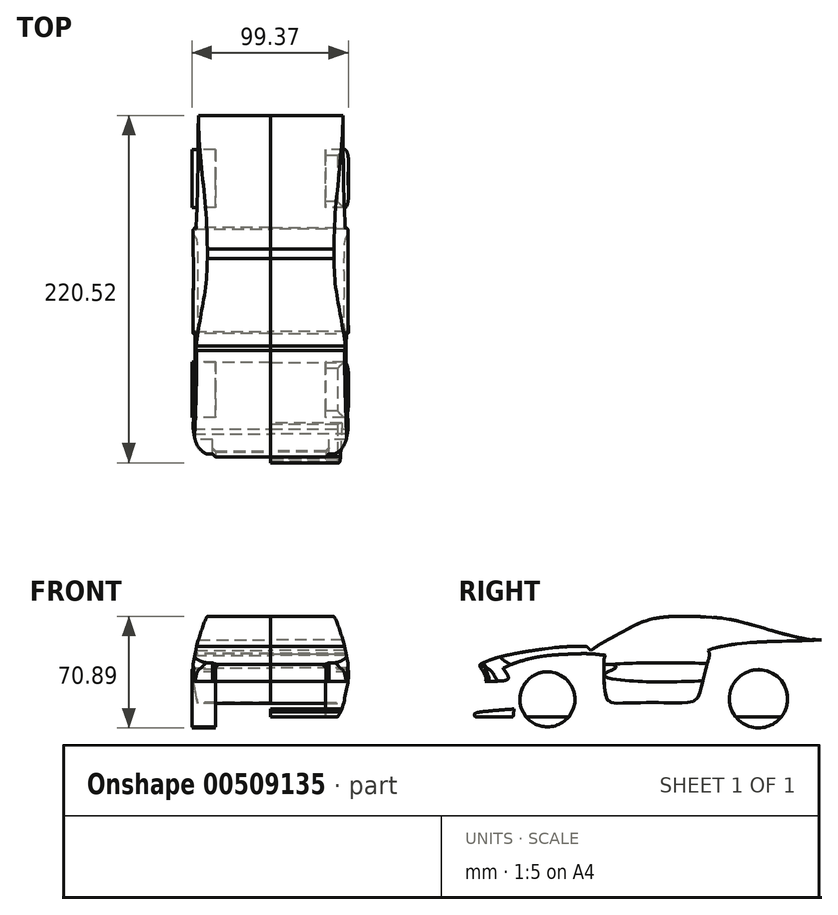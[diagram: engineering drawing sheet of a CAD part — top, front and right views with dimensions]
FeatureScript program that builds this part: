
annotation { "Feature Type Name" : "Feature", "Feature Type Description" : "" }
export const myFeature = defineFeature(function(context is Context, id is Id, definition is map)
    precondition{}
    {
        {
            var Q0;
            Q0=qCreatedBy(makeId("Right.planeOp"),FACE);
            var sketch = newSketch(context, id + "F0", { "sketchPlane" : qUnion([Q0])});
            skFitSpline(sketch, "E0", {"points": [v(-115.12, 3.89) * mm, v(-110.53, 5.87) * mm, v(-104.21, 8.1) * mm, v(-95.3, 10.2) * mm, v(-89.47, 11.32) * mm, v(-81.92, 12.56) * mm, v(-71.02, 14.05) * mm, v(-60.11, 15.04) * mm, v(-47.6, 15.16) * mm], "startDerivative": vector(46.35, 20.6) * mm, "endDerivative": vector(83.86, -0.63) * mm});
            skFitSpline(sketch, "E1", {"points": [v(-115.12, 3.89) * mm, v(-115.12, 2.28) * mm, v(-113.63, 0) * mm, v(-112.27, -2.68) * mm, v(-111.4, -5.03) * mm, v(-112.02, -6.89) * mm, v(-115.12, -7.26) * mm, v(-117.1, -8) * mm, v(-117.6, -10.98) * mm, v(-116.85, -14.07) * mm, v(-115.12, -17.91) * mm, v(-113.63, -22.75) * mm, v(-113.63, -25.84) * mm, v(-118.46, -27.45) * mm, v(-118.46, -29.19) * mm, v(-116.23, -29.44) * mm], "startDerivative": vector(-5.56, -32) * mm, "endDerivative": vector(44.62, 5.26) * mm});
            skFitSpline(sketch, "E2", {"points": [v(-116.23, -29.44) * mm, v(-112.64, -29.44) * mm, v(-107.06, -29.44) * mm, v(-97.77, -29.44) * mm, v(-94.18, -29.44) * mm], "startDerivative": vector(16.96, 0) * mm, "endDerivative": vector(14.87, 0) * mm});
            skLineSegment(sketch, "E3", {"start": v(-94.18, -29.44) * mm, "end": v(-92.7, -17.17) * mm});
            skArc(sketch, "E4", {"start": v(-92.7, -17.17) * mm, "mid": v(-71.99, 0.79) * mm, "end": v(-52.06, -18.04) * mm});
            skLineSegment(sketch, "E5", {"start": v(-52.06, -18.04) * mm, "end": v(-51.2, -29.07) * mm});
            skLineSegment(sketch, "E6", {"start": v(-51.2, -29.07) * mm, "end": v(-6.1, -29.07) * mm});
            skLineSegment(sketch, "E7", {"start": v(-6.1, -29.07) * mm, "end": v(31.32, -29.07) * mm});
            skLineSegment(sketch, "E8", {"start": v(31.32, -29.07) * mm, "end": v(40.99, -28.04) * mm});
            skLineSegment(sketch, "E9", {"start": v(40.99, -28.04) * mm, "end": v(40.99, -17.13) * mm});
            skArc(sketch, "E10", {"start": v(40.99, -17.13) * mm, "mid": v(61.47, 3.54) * mm, "end": v(82.33, -16.75) * mm});
            skLineSegment(sketch, "E11", {"start": v(82.33, -16.75) * mm, "end": v(83.68, -23.62) * mm});
            skLineSegment(sketch, "E12", {"start": v(83.68, -23.62) * mm, "end": v(106.37, -19.15) * mm});
            skLineSegment(sketch, "E13", {"start": v(106.37, -19.15) * mm, "end": v(106.5, -19.77) * mm});
            skLineSegment(sketch, "E14", {"start": v(114.07, 4.94) * mm, "end": v(107.96, 16.5) * mm});
            skFitSpline(sketch, "E15", {"points": [v(-47.6, 15.16) * mm, v(-44.76, 12.7) * mm], "startDerivative": vector(2.84, -2.47) * mm, "endDerivative": vector(2.84, -2.47) * mm});
            skFitSpline(sketch, "E16", {"points": [v(-44.76, 12.7) * mm, v(-37, 17.79) * mm, v(-22.88, 25.43) * mm, v(-12.46, 30.64) * mm, v(0, 33.65) * mm, v(17.06, 34.34) * mm, v(30.96, 33.76) * mm, v(49.02, 31.22) * mm, v(92.9, 19.87) * mm, v(106.32, 18.71) * mm, v(107.96, 16.5) * mm], "startDerivative": vector(87.2, 61.22) * mm, "endDerivative": vector(25.17, -59.7) * mm});
            skFitSpline(sketch, "E17", {"points": [v(101.69, 19.38) * mm, v(111.42, 21.14) * mm, v(111.18, 19.3) * mm, v(109.56, 18.13) * mm, v(107.96, 16.5) * mm], "startDerivative": vector(39.45, 2.67) * mm, "endDerivative": vector(-7.42, -9.04) * mm});
            skFitSpline(sketch, "E18", {"points": [v(106.37, -19.15) * mm, v(108.98, -15.43) * mm, v(111.7, -12.94) * mm, v(114.48, -11.03) * mm, v(114.88, -6.23) * mm, v(114.82, 0) * mm, v(114.07, 4.94) * mm], "startDerivative": vector(15.34, 23.5) * mm, "endDerivative": vector(-5.54, 27.42) * mm});
            skFitSpline(sketch, "E19", {"points": [v(-113.12, 4.77) * mm, v(-111.87, 2.87) * mm, v(-110.32, 1.07) * mm, v(-105.98, 0.87) * mm, v(-100.5, 1.48) * mm, v(-96.32, 3.36) * mm, v(-79.86, 8.24) * mm, v(-61.04, 10.2) * mm, v(-47.12, 11.47) * mm, v(-44.76, 12.7) * mm], "startDerivative": vector(19.68, -28.39) * mm, "endDerivative": vector(25.59, 19.1) * mm});
            skFitSpline(sketch, "E20", {"points": [v(-112.02, -6.89) * mm, v(-105.37, -6.89) * mm, v(-98.43, -6.17) * mm, v(-97.21, -4.7) * mm, v(-98.82, -1.2) * mm, v(-100.5, 1.48) * mm], "startDerivative": vector(25.22, -0.18) * mm, "endDerivative": vector(-8.95, 14.4) * mm});
            skFitSpline(sketch, "E21", {"points": [v(-110.32, 1.07) * mm, v(-107.92, -0.62) * mm, v(-105.2, -4.95) * mm, v(-104.07, -6.87) * mm], "startDerivative": vector(7.72, -3.95) * mm, "endDerivative": vector(3.65, -5.92) * mm});
            skFitSpline(sketch, "E22", {"points": [v(-102.37, -6.8) * mm, v(-102.43, 1.14) * mm], "startDerivative": vector(-0.06, 8) * mm, "endDerivative": vector(-0.06, 8) * mm});
            skFitSpline(sketch, "E23", {"points": [v(-114.87, -26.38) * mm, v(-109.28, -25.84) * mm, v(-95.95, -24.7) * mm, v(-93.6, -24.62) * mm], "startDerivative": vector(14.47, 1.38) * mm, "endDerivative": vector(8.46, -0.02) * mm});
            skFitSpline(sketch, "E24", {"points": [v(-34.64, 11.1) * mm, v(-36.3, 7.8) * mm, v(-36.57, 2.3) * mm, v(-36.43, -5) * mm, v(-35.88, -12.71) * mm, v(-33.68, -19.46) * mm, v(-27.24, -20.86) * mm, v(-5.92, -20.47) * mm, v(16.57, -20.37) * mm, v(22.12, -18.62) * mm, v(24.85, -12.58) * mm, v(29.03, 3.87) * mm, v(30.4, 11.17) * mm, v(28.93, 14.48) * mm, v(30.59, 21.88) * mm, v(31.66, 25.58) * mm, v(31.56, 27.92) * mm, v(28.15, 28.89) * mm, v(15.99, 29.76) * mm, v(-3.48, 28.89) * mm, v(-15.85, 24.5) * mm, v(-32.4, 13.12) * mm, v(-34.64, 11.1) * mm]});
            skFitSpline(sketch, "E25", {"points": [v(101.69, 19.38) * mm, v(85.1, 18.71) * mm, v(53.76, 17.4) * mm, v(32.63, 13.8) * mm, v(20.56, 10.49) * mm, v(-30.26, 9.22) * mm, v(-44.76, 10.49) * mm, v(-55.1, 10.5) * mm], "startDerivative": vector(-118.1, -5.72) * mm, "endDerivative": vector(-105.53, -2.56) * mm});
            skCircle(sketch, "E26", {"center": v(-72.42, -18.4) * mm, "radius": 17.5 * mm});
            skCircle(sketch, "E27", {"center": v(61.66, -18.05) * mm, "radius": 18.5 * mm});
            skSolve(sketch);
        }
        {
            var Q0;
            {var subQ3=sQuery(id+"F0.wireOp",EDGE,"E21");Q0=makeQuery(id+"F0.imprint","IMPRINT",FACE,{"disambiguationData":[TD([[makeQuery(id+"F0.imprint","IMPRINT",EDGE,{"derivedFrom":subQ3}),-1.0]])]});}
            var Q1;
            {var subQ0=sQuery(id+"F0.wireOp",EDGE,"E21");Q1=makeQuery(id+"F0.imprint","IMPRINT",FACE,{"disambiguationData":[TD([[makeQuery(id+"F0.imprint","IMPRINT",EDGE,{"derivedFrom":subQ0}),1.0]])]});}
            var Q2;
            {var subQ3=sQuery(id+"F0.wireOp",EDGE,"E22");Q2=makeQuery(id+"F0.imprint","IMPRINT",FACE,{"disambiguationData":[TD([[makeQuery(id+"F0.imprint","IMPRINT",EDGE,{"derivedFrom":subQ3}),-1.0]])]});}
            var Q3;
            {var subQ11=sQuery(id+"F0.wireOp",EDGE,"E4");Q3=makeQuery(id+"F0.imprint","IMPRINT",FACE,{"disambiguationData":[TD([[makeQuery(id+"F0.imprint","IMPRINT",EDGE,{"derivedFrom":subQ11}),1.0]])]});}
            var Q4;
            {var subQ0=sQuery(id+"F0.wireOp",EDGE,"E25");var subQ1=sQuery(id+"F0.wireOp",EDGE,"E24");var subQ2=makeQuery(id+"F0.imprint","INTERSECT",VERTEX,{"disambiguationData":[OD(0.0)],"derivedFrom":[subQ1,subQ0]});Q4=makeQuery(id+"F0.imprint","IMPRINT",FACE,{"disambiguationData":[TD([[makeQuery(id+"F0.imprint","IMPRINT",EDGE,{"disambiguationData":[TD([[subQ2,1.0]])],"derivedFrom":subQ1}),1.0]])]});}
            var Q5;
            {var subQ1=sQuery(id+"F0.wireOp",EDGE,"E16");Q5=makeQuery(id+"F0.imprint","IMPRINT",FACE,{"disambiguationData":[TD([[makeQuery(id+"F0.imprint","IMPRINT",EDGE,{"derivedFrom":subQ1}),-1.0]])]});}
            var Q6;
            {var subQ0=sQuery(id+"F0.wireOp",EDGE,"E25");var subQ1=sQuery(id+"F0.wireOp",EDGE,"E24");var subQ2=makeQuery(id+"F0.imprint","INTERSECT",VERTEX,{"disambiguationData":[OD(0.0)],"derivedFrom":[subQ1,subQ0]});Q6=makeQuery(id+"F0.imprint","IMPRINT",FACE,{"disambiguationData":[TD([[makeQuery(id+"F0.imprint","IMPRINT",EDGE,{"disambiguationData":[TD([[subQ2,-1.0]])],"derivedFrom":subQ1}),1.0]])]});}
            var Q7;
            {var subQ5=sQuery(id+"F0.wireOp",EDGE,"E15");Q7=makeQuery(id+"F0.imprint","IMPRINT",FACE,{"disambiguationData":[TD([[makeQuery(id+"F0.imprint","IMPRINT",EDGE,{"derivedFrom":subQ5}),-1.0]])]});}
            extrude(context, id + "F1", {"entities" : qUnion([Q0, Q1, Q2, Q3, Q4, Q5, Q6, Q7]), "depth" : 50 * mm, "offsetDistance" : 25 * mm});
        }
        {
            var Q0;
            Q0=qCreatedBy(makeId("Front.planeOp"),FACE);
            var sketch = newSketch(context, id + "F2", { "sketchPlane" : qUnion([Q0])});
            skFitSpline(sketch, "E28", {"points": [v(40.2, 34.34) * mm, v(43.6, 26.25) * mm, v(46.63, 16.71) * mm, v(49.3, 3.89) * mm], "startDerivative": vector(18.15, -29.72) * mm, "endDerivative": vector(8.92, -39.22) * mm});
            skFitSpline(sketch, "E29", {"points": [v(49.3, 3.89) * mm, v(49.3, -5.43) * mm, v(47.33, -16.23) * mm, v(45.53, -23.84) * mm, v(42.58, -29.44) * mm], "startDerivative": vector(-1.8, -37.23) * mm, "endDerivative": vector(-15.66, -24.5) * mm});
            skLineSegment(sketch, "E30", {"start": v(40.2, 34.34) * mm, "end": v(0, 34.34) * mm});
            skLineSegment(sketch, "E31", {"start": v(0, 34.34) * mm, "end": v(0, 46.52) * mm});
            skLineSegment(sketch, "E32", {"start": v(0, 46.52) * mm, "end": v(62.63, 46.52) * mm});
            skLineSegment(sketch, "E33", {"start": v(62.63, 46.52) * mm, "end": v(62.63, -39.27) * mm});
            skLineSegment(sketch, "E34", {"start": v(62.63, -39.27) * mm, "end": v(0, -39.27) * mm});
            skLineSegment(sketch, "E35", {"start": v(0, -39.27) * mm, "end": v(0, -29.44) * mm});
            skLineSegment(sketch, "E36", {"start": v(0, -29.44) * mm, "end": v(42.58, -29.44) * mm});
            skSolve(sketch);
        }
        {
            var Q0;
            {var subQ3=sQuery(id+"F0.wireOp",EDGE,"E21");Q0=makeQuery(id+"F0.imprint","IMPRINT",FACE,{"disambiguationData":[TD([[makeQuery(id+"F0.imprint","IMPRINT",EDGE,{"derivedFrom":subQ3}),-1.0]])]});}
            extrude(context, id + "F3", {"entities" : qUnion([Q0]), "operationType" : NewBodyOperationType.REMOVE, "depth" : 50 * mm, "offsetDistance" : 25 * mm});
        }
        {
            var Q0;
            {var subQ3=sQuery(id+"F0.wireOp",EDGE,"E21");Q0=makeQuery(id+"F0.imprint","IMPRINT",FACE,{"disambiguationData":[TD([[makeQuery(id+"F0.imprint","IMPRINT",EDGE,{"derivedFrom":subQ3}),-1.0]])]});}
            extrude(context, id + "F4", {"entities" : qUnion([Q0]), "operationType" : NewBodyOperationType.ADD, "depth" : 37 * mm, "offsetDistance" : 25 * mm});
        }
        {
            var Q0;
            Q0=makeQuery(id+"F4.opExtrude","CAP_EDGE",EDGE,{"disambiguationData":[OSD([sQuery(id+"F0.wireOp",EDGE,"E1")])],"isStart":false});
            chamfer(context, id + "F5", {"entities" : qUnion([Q0]), "width" : 1.95 * mm, "tangentPropagation" : true});
        }
        {
            var Q0;
            Q0=qCreatedBy(makeId("Top.planeOp"),FACE);
            var sketch = newSketch(context, id + "F6", { "sketchPlane" : qUnion([Q0])});
            skFitSpline(sketch, "E37", {"points": [v(0, -118.67) * mm, v(27.97, -116.22) * mm, v(43.7, -111.3) * mm, v(48.78, -100.04) * mm, v(49.87, -68.79) * mm, v(49.15, -16.82) * mm, v(49.23, 37.37) * mm, v(49.45, 63.73) * mm, v(49.15, 90.74) * mm, v(47.33, 102.73) * mm, v(45.5, 108.04) * mm, v(39.13, 112.3) * mm, v(26.33, 114.9) * mm, v(0, 114.82) * mm], "startDerivative": vector(301.62, 3.64) * mm, "endDerivative": vector(-332.6, 15.34) * mm});
            skLineSegment(sketch, "E38", {"start": v(0, -118.67) * mm, "end": v(0, -134.1) * mm});
            skLineSegment(sketch, "E39", {"start": v(0, -134.1) * mm, "end": v(113.53, -134.1) * mm});
            skLineSegment(sketch, "E40", {"start": v(113.53, -134.1) * mm, "end": v(113.53, 157) * mm});
            skLineSegment(sketch, "E41", {"start": v(113.53, 157) * mm, "end": v(0, 157) * mm});
            skLineSegment(sketch, "E42", {"start": v(0, 157) * mm, "end": v(0, 114.82) * mm});
            skSolve(sketch);
        }
        {
            var Q0;
            Q0=makeQuery(id+"F6.imprint","IMPRINT",FACE,{"disambiguationData":[TD([[makeQuery(id+"F6.imprint","IMPRINT",EDGE,{"derivedFrom":sQuery(id+"F6.wireOp",EDGE,"E37")}),-1.0]])]});
            extrude(context, id + "F7", {"entities" : qUnion([Q0]), "operationType" : NewBodyOperationType.REMOVE, "endBound" : BoundingType.SYMMETRIC, "oppositeDirection" : true, "depth" : 80 * mm, "offsetDistance" : 25 * mm});
        }
        {
            var Q0;
            {var subQ0=sQuery(id+"F0.wireOp",EDGE,"E2");Q0=makeQuery(id+"F0.imprint","IMPRINT",FACE,{"disambiguationData":[TD([[makeQuery(id+"F0.imprint","IMPRINT",EDGE,{"derivedFrom":subQ0}),1.0]])]});}
            extrude(context, id + "F8", {"entities" : qUnion([Q0]), "operationType" : NewBodyOperationType.ADD, "depth" : 48 * mm, "offsetDistance" : 25 * mm});
        }
        {
            var Q0;
            Q0=makeQuery(id+"F0.imprint","IMPRINT",FACE,{"disambiguationData":[TD([[makeQuery(id+"F0.imprint","IMPRINT",EDGE,{"derivedFrom":sQuery(id+"F0.wireOp",EDGE,"E26")}),1.0]])]});
            var Q1;
            Q1=makeQuery(id+"F0.imprint","IMPRINT",FACE,{"disambiguationData":[TD([[makeQuery(id+"F0.imprint","IMPRINT",EDGE,{"derivedFrom":sQuery(id+"F0.wireOp",EDGE,"E27")}),1.0]])]});
            extrude(context, id + "F9", {"entities" : qUnion([Q0, Q1]), "endBound" : BoundingType.SYMMETRIC, "depth" : 100 * mm, "offsetDistance" : 25 * mm});
        }
        {
            var Q0;
            Q0=makeQuery(id+"F0.imprint","IMPRINT",FACE,{"disambiguationData":[TD([[makeQuery(id+"F0.imprint","IMPRINT",EDGE,{"derivedFrom":sQuery(id+"F0.wireOp",EDGE,"E26")}),1.0]])]});
            var Q1;
            Q1=makeQuery(id+"F0.imprint","IMPRINT",FACE,{"disambiguationData":[TD([[makeQuery(id+"F0.imprint","IMPRINT",EDGE,{"derivedFrom":sQuery(id+"F0.wireOp",EDGE,"E27")}),1.0]])]});
            extrude(context, id + "F10", {"entities" : qUnion([Q0, Q1]), "operationType" : NewBodyOperationType.REMOVE, "endBound" : BoundingType.SYMMETRIC, "oppositeDirection" : true, "depth" : 70 * mm, "offsetDistance" : 25 * mm});
        }
        {
            var Q0;
            Q0=makeQuery(id+"F2.imprint","IMPRINT",FACE,{"disambiguationData":[TD([[makeQuery(id+"F2.imprint","IMPRINT",EDGE,{"derivedFrom":sQuery(id+"F2.wireOp",EDGE,"E28")}),1.0]])]});
            extrude(context, id + "F11", {"entities" : qUnion([Q0]), "operationType" : NewBodyOperationType.REMOVE, "endBound" : BoundingType.SYMMETRIC, "oppositeDirection" : true, "depth" : 240 * mm, "offsetDistance" : 25 * mm});
        }
        {
            var Q0;
            Q0=makeQuery(id+"F1.opExtrude","SWEPT_BODY",BODY,{"disambiguationData":[OSD([sQuery(id+"F0.wireOp",EDGE,"E0"),sQuery(id+"F0.wireOp",EDGE,"E1"),sQuery(id+"F0.wireOp",EDGE,"E3"),sQuery(id+"F0.wireOp",EDGE,"E4"),sQuery(id+"F0.wireOp",EDGE,"E5"),sQuery(id+"F0.wireOp",EDGE,"E6"),sQuery(id+"F0.wireOp",EDGE,"E7"),sQuery(id+"F0.wireOp",EDGE,"E8"),sQuery(id+"F0.wireOp",EDGE,"E9"),sQuery(id+"F0.wireOp",EDGE,"E10"),sQuery(id+"F0.wireOp",EDGE,"E11"),sQuery(id+"F0.wireOp",EDGE,"E12"),sQuery(id+"F0.wireOp",EDGE,"E14"),sQuery(id+"F0.wireOp",EDGE,"E15"),sQuery(id+"F0.wireOp",EDGE,"E16"),sQuery(id+"F0.wireOp",EDGE,"E17"),sQuery(id+"F0.wireOp",EDGE,"E18"),sQuery(id+"F0.wireOp",EDGE,"E23")])]});
            var Q1;
            Q1=qCreatedBy(makeId("Right.planeOp"),FACE);
            mirror(context, id + "F12", {"operationType" : NewBodyOperationType.ADD, "entities" : qUnion([Q0]), "mirrorPlane" : qUnion([Q1])});
        }
    });
